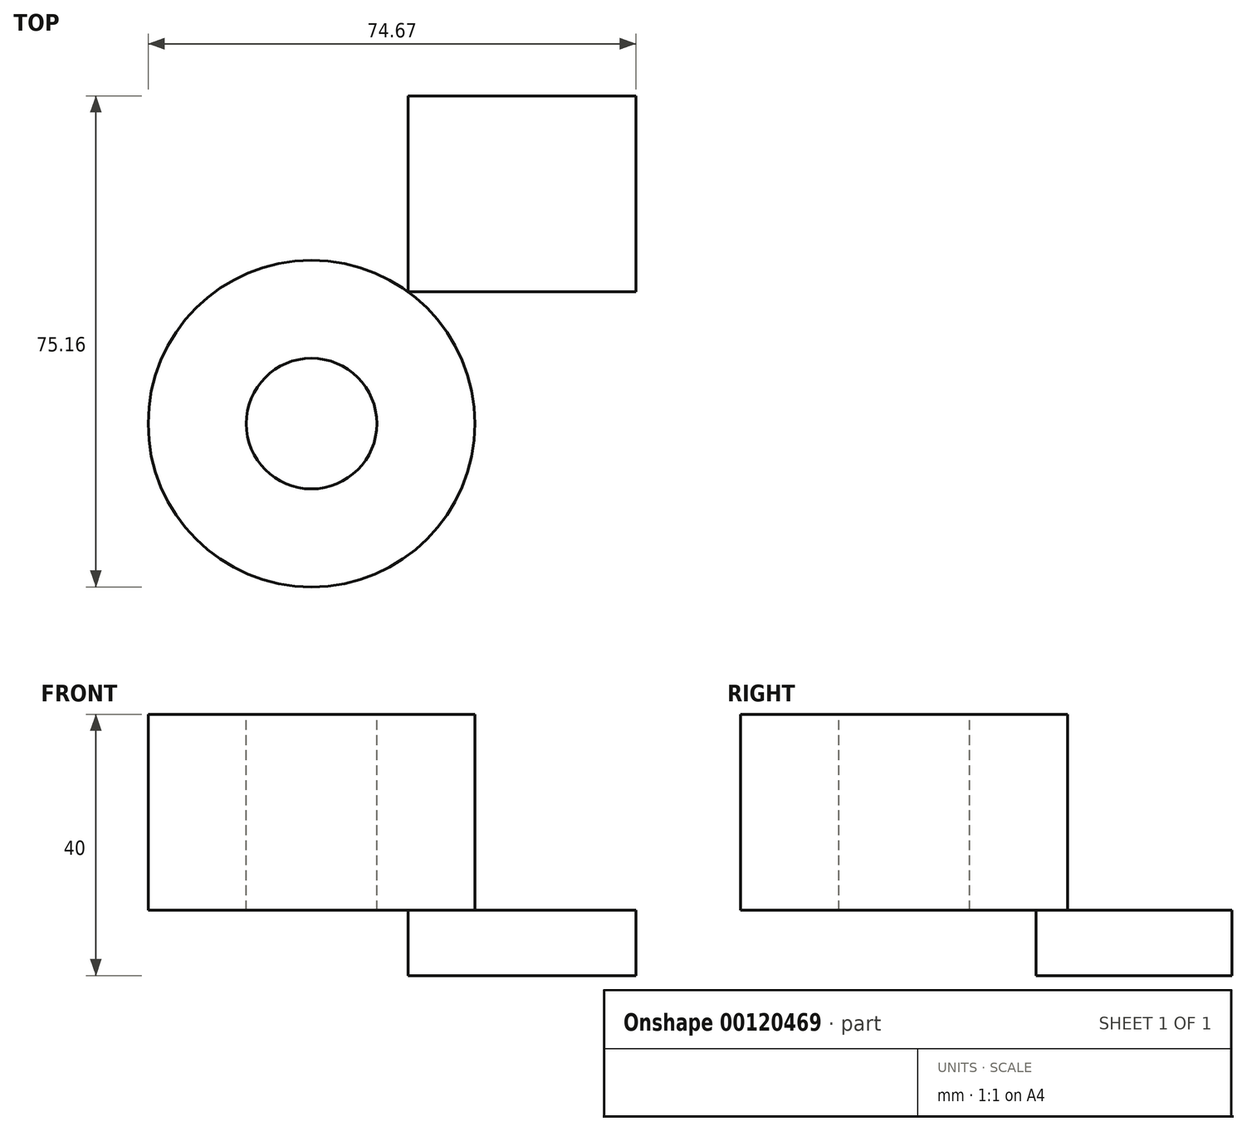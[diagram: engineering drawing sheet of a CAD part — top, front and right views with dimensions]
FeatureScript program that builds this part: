
annotation { "Feature Type Name" : "Feature", "Feature Type Description" : "" }
export const myFeature = defineFeature(function(context is Context, id is Id, definition is map)
    precondition{}
    {
        {
            var Q0;
            Q0=qCreatedBy(makeId("Top.planeOp"),FACE);
            var sketch = newSketch(context, id + "F0", { "sketchPlane" : qUnion([Q0])});
            skCircle(sketch, "E0", {"center": v(0, 0) * mm, "radius": 25 * mm});
            skCircle(sketch, "E1", {"center": v(0, 0) * mm, "radius": 10 * mm});
            skSolve(sketch);
        }
        {
            var Q0;
            Q0=makeQuery(id+"F0.imprint","IMPRINT",FACE,{"disambiguationData":[TD([[makeQuery(id+"F0.imprint","IMPRINT",EDGE,{"derivedFrom":sQuery(id+"F0.wireOp",EDGE,"E0")}),1.0]])]});
            extrude(context, id + "F1", {"entities" : qUnion([Q0]), "oppositeDirection" : true, "depth" : 30 * mm});
        }
        {
            var Q0;
            Q0=makeQuery(id+"F1.opExtrude","CAP_FACE",FACE,{"disambiguationData":[OSD([sQuery(id+"F0.wireOp",EDGE,"E0"),sQuery(id+"F0.wireOp",EDGE,"E1")])],"isStart":false});
            var sketch = newSketch(context, id + "F2", { "sketchPlane" : qUnion([Q0])});
            skLineSegment(sketch, "E2", {"start": v(14.78, -20.16) * mm, "end": v(49.67, -20.16) * mm});
            skLineSegment(sketch, "E3", {"start": v(49.67, -20.16) * mm, "end": v(49.67, -50.16) * mm});
            skLineSegment(sketch, "E4", {"start": v(49.67, -50.16) * mm, "end": v(14.78, -50.16) * mm});
            skLineSegment(sketch, "E5", {"start": v(14.78, -50.16) * mm, "end": v(14.78, -20.16) * mm});
            skSolve(sketch);
        }
        {
            var Q0;
            Q0 = qSketchRegion(id + "F2", true);
            extrude(context, id + "F3", {"entities" : qUnion([Q0]), "depth" : 10 * mm});
        }
    });
